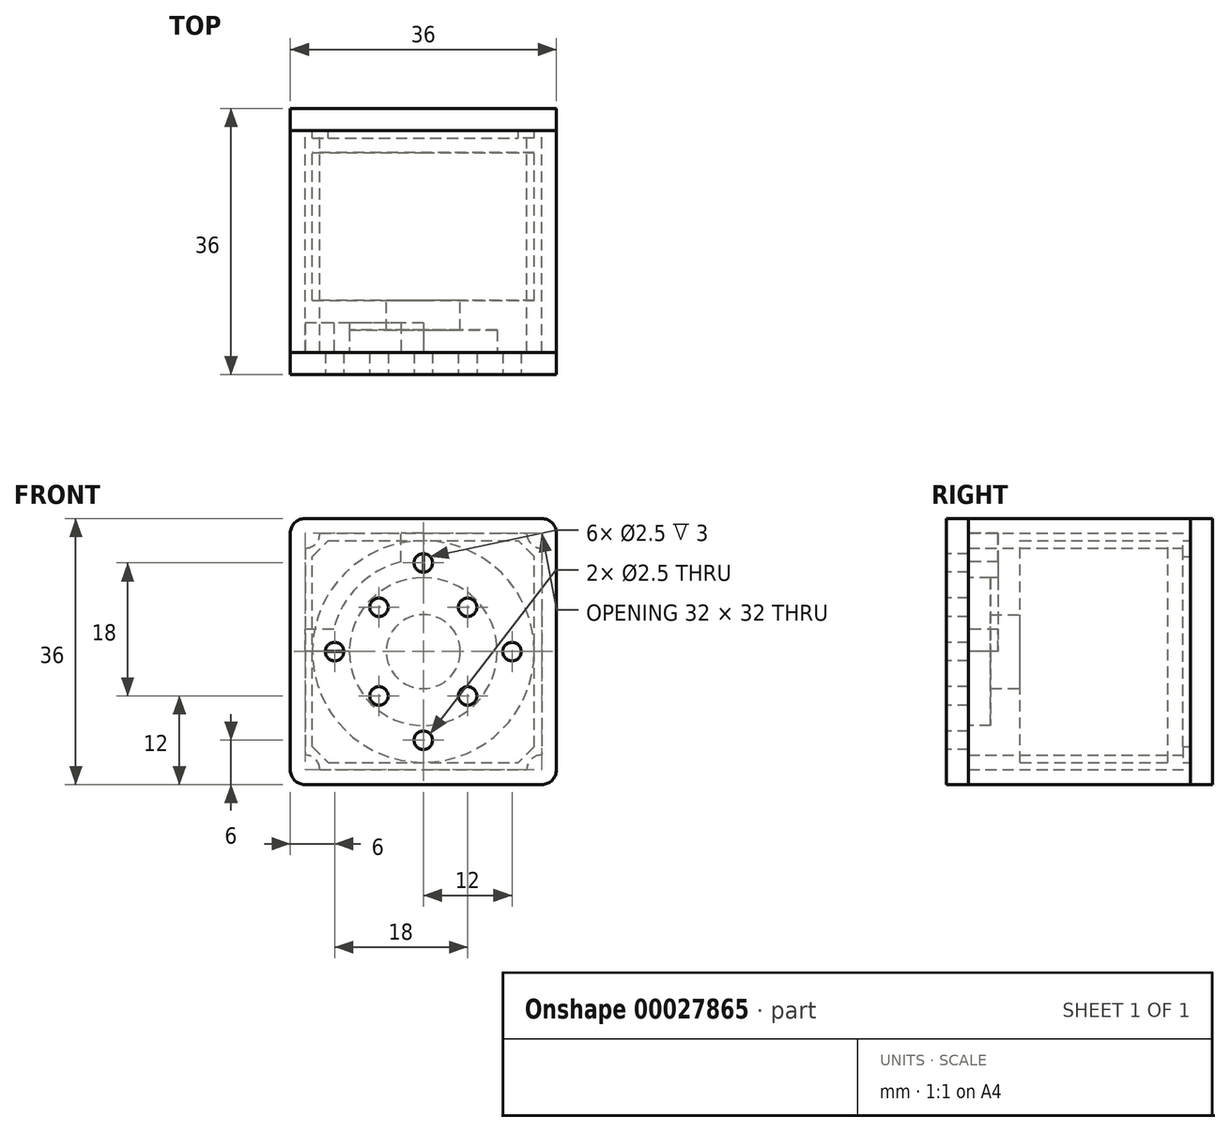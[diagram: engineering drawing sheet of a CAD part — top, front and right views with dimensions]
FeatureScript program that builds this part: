
annotation { "Feature Type Name" : "Feature", "Feature Type Description" : "" }
export const myFeature = defineFeature(function(context is Context, id is Id, definition is map)
    precondition{}
    {
        {
            var Q0;
            Q0=qCreatedBy(makeId("Front.planeOp"),FACE);
            var sketch = newSketch(context, id + "F0", { "sketchPlane" : qUnion([Q0])});
            skLineSegment(sketch, "E0.rect.bottom", {"start": v(18, -18) * mm, "end": v(-18, -18) * mm});
            skLineSegment(sketch, "E0.rect.top", {"start": v(18, 18) * mm, "end": v(-18, 18) * mm});
            skLineSegment(sketch, "E0.rect.left", {"start": v(18, -18) * mm, "end": v(18, 18) * mm});
            skLineSegment(sketch, "E0.rect.right", {"start": v(-18, -18) * mm, "end": v(-18, 18) * mm});
            skPoint(sketch, "E0.rect.middle", {"position": v(0, 0) * mm});
            skCircle(sketch, "E1", {"center": v(0, 0) * mm, "radius": 8.49 * mm, "construction": true});
            skLineSegment(sketch, "E2.rect.bottom", {"start": v(-6, 6) * mm, "end": v(6, 6) * mm, "construction": true});
            skLineSegment(sketch, "E2.rect.top", {"start": v(-6, -6) * mm, "end": v(6, -6) * mm, "construction": true});
            skLineSegment(sketch, "E2.rect.left", {"start": v(-6, 6) * mm, "end": v(-6, -6) * mm, "construction": true});
            skLineSegment(sketch, "E2.rect.right", {"start": v(6, 6) * mm, "end": v(6, -6) * mm, "construction": true});
            skCircle(sketch, "E3", {"center": v(-6, 6) * mm, "radius": 1.25 * mm});
            skCircle(sketch, "E4", {"center": v(6, 6) * mm, "radius": 1.25 * mm});
            skCircle(sketch, "E5", {"center": v(6, -6) * mm, "radius": 1.25 * mm});
            skCircle(sketch, "E6", {"center": v(-6, -6) * mm, "radius": 1.25 * mm});
            skCircle(sketch, "E7", {"center": v(0, 0) * mm, "radius": 12 * mm, "construction": true});
            skCircle(sketch, "E8", {"center": v(0, 12) * mm, "radius": 1.25 * mm});
            skCircle(sketch, "E9.1.0", {"center": v(-12, 0) * mm, "radius": 1.25 * mm});
            skCircle(sketch, "E9.2.0", {"center": v(0, -12) * mm, "radius": 1.25 * mm});
            skCircle(sketch, "E9.3.0", {"center": v(12, 0) * mm, "radius": 1.25 * mm});
            skCircle(sketch, "E10", {"center": v(0, 0) * mm, "radius": 15 * mm});
            skSolve(sketch);
        }
        {
            var Q0;
            Q0=qCreatedBy(makeId("Front.planeOp"),FACE);
            var sketch = newSketch(context, id + "F1", { "sketchPlane" : qUnion([Q0])});
            skLineSegment(sketch, "E11.rect.bottom", {"start": v(-16, 18) * mm, "end": v(0, 18) * mm});
            skLineSegment(sketch, "E11.rect.left", {"start": v(-18, 16) * mm, "end": v(-18, 0) * mm});
            skPoint(sketch, "E11.rect.middle", {"position": v(0, 0) * mm});
            skLineSegment(sketch, "E12.0", {"start": v(0, 16) * mm, "end": v(-14, 16) * mm});
            skLineSegment(sketch, "E12.3", {"start": v(-16, 0) * mm, "end": v(-16, 14) * mm});
            skArc(sketch, "E13", {"start": v(-16, 14) * mm, "mid": v(-14.59, 14.59) * mm, "end": v(-14, 16) * mm});
            skLineSegment(sketch, "E14", {"start": v(0, 18) * mm, "end": v(0, 0) * mm, "construction": true});
            skLineSegment(sketch, "E15", {"start": v(-18, 0) * mm, "end": v(0, 0) * mm, "construction": true});
            skPoint(sketch, "E16.visualSharp", {"position": v(-18, 18) * mm});
            skArc(sketch, "E16.filletArc", {"start": v(-16, 18) * mm, "mid": v(-17.41, 17.41) * mm, "end": v(-18, 16) * mm});
            skLineSegment(sketch, "E17", {"start": v(0, 18) * mm, "end": v(0, 16) * mm});
            skLineSegment(sketch, "E18", {"start": v(-18, 0) * mm, "end": v(-16, 0) * mm});
            skSolve(sketch);
        }
        {
            var Q0;
            Q0=qCreatedBy(makeId("Front.planeOp"),FACE);
            var sketch = newSketch(context, id + "F2", { "sketchPlane" : qUnion([Q0])});
            skArc(sketch, "E19", {"start": v(-7.07, 7.07) * mm, "mid": v(-9.24, 3.83) * mm, "end": v(-10, 0) * mm});
            skArc(sketch, "E20", {"start": v(-8.84, 8.84) * mm, "mid": v(-10.89, 6.14) * mm, "end": v(-12.13, 3) * mm});
            skLineSegment(sketch, "E21", {"start": v(-12.13, 3) * mm, "end": v(-16, 3) * mm});
            skLineSegment(sketch, "E22", {"start": v(-16, 0) * mm, "end": v(-16, 3) * mm});
            skLineSegment(sketch, "E23", {"start": v(-16, 16) * mm, "end": v(0, 0) * mm, "construction": true});
            skLineSegment(sketch, "E24", {"start": v(-16, 0) * mm, "end": v(0, 0) * mm, "construction": true});
            skArc(sketch, "E25.0.MirrorCS", {"start": v(-8.84, 8.84) * mm, "mid": v(-6.14, 10.89) * mm, "end": v(-3, 12.13) * mm});
            skLineSegment(sketch, "E26.0.MirrorCS", {"start": v(-3, 12.13) * mm, "end": v(-3, 16) * mm});
            skLineSegment(sketch, "E27.0.MirrorCS", {"start": v(0, 16) * mm, "end": v(-3, 16) * mm});
            skArc(sketch, "E28.0.MirrorCS", {"start": v(-7.07, 7.07) * mm, "mid": v(-3.83, 9.24) * mm, "end": v(0, 10) * mm});
            skLineSegment(sketch, "E29", {"start": v(0, 16) * mm, "end": v(0, 10) * mm});
            skLineSegment(sketch, "E30", {"start": v(-10, 0) * mm, "end": v(-16, 0) * mm});
            skSolve(sketch);
        }
        {
            var Q0;
            Q0=qSketchRegion(id+"F1",true);
            extrude(context, id + "F3", {"entities" : qUnion([Q0]), "endBound" : BoundingType.SYMMETRIC, "depth" : 30 * mm});
        }
        {
            var Q0;
            Q0=makeQuery(id+"F3.opExtrude","CAP_FACE",FACE,{"disambiguationData":[OSD([sQuery(id+"F1.wireOp",EDGE,"E11.rect.bottom"),sQuery(id+"F1.wireOp",EDGE,"E11.rect.left"),sQuery(id+"F1.wireOp",EDGE,"E12.0"),sQuery(id+"F1.wireOp",EDGE,"E12.3"),sQuery(id+"F1.wireOp",EDGE,"E13"),sQuery(id+"F1.wireOp",EDGE,"E16.filletArc"),sQuery(id+"F1.wireOp",EDGE,"E17"),sQuery(id+"F1.wireOp",EDGE,"E18")])],"isStart":false});
            var sketch = newSketch(context, id + "F4", { "sketchPlane" : qUnion([Q0])});
            skArc(sketch, "E31.0.0", {"start": v(-7.07, 7.07) * mm, "mid": v(-9.24, 3.83) * mm, "end": v(-10, 0) * mm});
            skArc(sketch, "E31.0.1", {"start": v(-7.07, 7.07) * mm, "mid": v(-3.83, 9.24) * mm, "end": v(0, 10) * mm});
            skLineSegment(sketch, "E31.0.2", {"start": v(0, 16) * mm, "end": v(0, 10) * mm});
            skLineSegment(sketch, "E31.0.3", {"start": v(0, 16) * mm, "end": v(-3, 16) * mm});
            skLineSegment(sketch, "E31.0.4", {"start": v(-3, 12.13) * mm, "end": v(-3, 16) * mm});
            skArc(sketch, "E31.0.5", {"start": v(-8.84, 8.84) * mm, "mid": v(-6.14, 10.89) * mm, "end": v(-3, 12.13) * mm});
            skArc(sketch, "E31.0.6", {"start": v(-8.84, 8.84) * mm, "mid": v(-10.89, 6.14) * mm, "end": v(-12.13, 3) * mm});
            skLineSegment(sketch, "E31.0.7", {"start": v(-12.13, 3) * mm, "end": v(-16, 3) * mm});
            skLineSegment(sketch, "E31.0.8", {"start": v(-16, 0) * mm, "end": v(-16, 3) * mm});
            skLineSegment(sketch, "E31.0.9", {"start": v(-10, 0) * mm, "end": v(-16, 0) * mm});
            skSolve(sketch);
        }
        {
            var Q0;
            Q0=qSketchRegion(id+"F4",true);
            extrude(context, id + "F5", {"entities" : qUnion([Q0]), "oppositeDirection" : true, "depth" : 4 * mm});
        }
        {
            var Q0;
            Q0=makeQuery(id+"F3.opExtrude","CAP_FACE",FACE,{"disambiguationData":[OSD([sQuery(id+"F1.wireOp",EDGE,"E11.rect.bottom"),sQuery(id+"F1.wireOp",EDGE,"E11.rect.left"),sQuery(id+"F1.wireOp",EDGE,"E12.0"),sQuery(id+"F1.wireOp",EDGE,"E12.3"),sQuery(id+"F1.wireOp",EDGE,"E13"),sQuery(id+"F1.wireOp",EDGE,"E16.filletArc"),sQuery(id+"F1.wireOp",EDGE,"E17"),sQuery(id+"F1.wireOp",EDGE,"E18")])],"isStart":true});
            var sketch = newSketch(context, id + "F6", { "sketchPlane" : qUnion([Q0])});
            skLineSegment(sketch, "E32", {"start": v(15, 0) * mm, "end": v(15, 12.88) * mm});
            skLineSegment(sketch, "E33", {"start": v(15, 12.88) * mm, "end": v(12.88, 15) * mm});
            skLineSegment(sketch, "E34", {"start": v(0, 15) * mm, "end": v(12.88, 15) * mm});
            skLineSegment(sketch, "E35", {"start": v(0, 15) * mm, "end": v(0, 0) * mm});
            skLineSegment(sketch, "E36", {"start": v(0, 0) * mm, "end": v(15, 0) * mm});
            skSolve(sketch);
        }
        {
            var Q0;
            Q0=qSketchRegion(id+"F6",true);
            extrude(context, id + "F7", {"entities" : qUnion([Q0]), "oppositeDirection" : true, "depth" : 1 * mm});
        }
        {
            var Q0;
            Q0=makeQuery(id+"F3.opExtrude","SWEPT_BODY",BODY,{"disambiguationData":[OSD([sQuery(id+"F1.wireOp",EDGE,"E11.rect.bottom"),sQuery(id+"F1.wireOp",EDGE,"E11.rect.left"),sQuery(id+"F1.wireOp",EDGE,"E12.0"),sQuery(id+"F1.wireOp",EDGE,"E12.3"),sQuery(id+"F1.wireOp",EDGE,"E13"),sQuery(id+"F1.wireOp",EDGE,"E16.filletArc"),sQuery(id+"F1.wireOp",EDGE,"E17"),sQuery(id+"F1.wireOp",EDGE,"E18")])]});
            var Q1;
            Q1=makeQuery(id+"F7.opExtrude","SWEPT_BODY",BODY,{"disambiguationData":[OSD([sQuery(id+"F6.wireOp",EDGE,"E32"),sQuery(id+"F6.wireOp",EDGE,"E33"),sQuery(id+"F6.wireOp",EDGE,"E34"),sQuery(id+"F6.wireOp",EDGE,"E35"),sQuery(id+"F6.wireOp",EDGE,"E36")])]});
            var Q2;
            Q2=qCreatedBy(makeId("Right.planeOp"),FACE);
            mirror(context, id + "F8", {"entities" : qUnion([Q0, Q1]), "mirrorPlane" : qUnion([Q2])});
        }
        {
            var Q0;
            Q0=makeQuery(id+"F8.opPattern","COPY",BODY,{"derivedFrom":makeQuery(id+"F3.opExtrude","SWEPT_BODY",BODY,{"disambiguationData":[OSD([sQuery(id+"F1.wireOp",EDGE,"E11.rect.bottom"),sQuery(id+"F1.wireOp",EDGE,"E11.rect.left"),sQuery(id+"F1.wireOp",EDGE,"E12.0"),sQuery(id+"F1.wireOp",EDGE,"E12.3"),sQuery(id+"F1.wireOp",EDGE,"E13"),sQuery(id+"F1.wireOp",EDGE,"E16.filletArc"),sQuery(id+"F1.wireOp",EDGE,"E17"),sQuery(id+"F1.wireOp",EDGE,"E18")])]}),"instanceName":"1"});
            var Q1;
            Q1=makeQuery(id+"F3.opExtrude","SWEPT_BODY",BODY,{"disambiguationData":[OSD([sQuery(id+"F1.wireOp",EDGE,"E11.rect.bottom"),sQuery(id+"F1.wireOp",EDGE,"E11.rect.left"),sQuery(id+"F1.wireOp",EDGE,"E12.0"),sQuery(id+"F1.wireOp",EDGE,"E12.3"),sQuery(id+"F1.wireOp",EDGE,"E13"),sQuery(id+"F1.wireOp",EDGE,"E16.filletArc"),sQuery(id+"F1.wireOp",EDGE,"E17"),sQuery(id+"F1.wireOp",EDGE,"E18")])]});
            var Q2;
            Q2=makeQuery(id+"F8.opPattern","COPY",BODY,{"derivedFrom":makeQuery(id+"F7.opExtrude","SWEPT_BODY",BODY,{"disambiguationData":[OSD([sQuery(id+"F6.wireOp",EDGE,"E32"),sQuery(id+"F6.wireOp",EDGE,"E33"),sQuery(id+"F6.wireOp",EDGE,"E34"),sQuery(id+"F6.wireOp",EDGE,"E35"),sQuery(id+"F6.wireOp",EDGE,"E36")])]}),"instanceName":"1"});
            var Q3;
            Q3=makeQuery(id+"F7.opExtrude","SWEPT_BODY",BODY,{"disambiguationData":[OSD([sQuery(id+"F6.wireOp",EDGE,"E32"),sQuery(id+"F6.wireOp",EDGE,"E33"),sQuery(id+"F6.wireOp",EDGE,"E34"),sQuery(id+"F6.wireOp",EDGE,"E35"),sQuery(id+"F6.wireOp",EDGE,"E36")])]});
            booleanBodies(context, id + "F9", {"operationType" : BooleanOperationType.UNION, "tools" : qUnion([Q0, Q1, Q2, Q3])});
        }
        {
            var Q0;
            Q0=makeQuery(id+"F8.opPattern","COPY",BODY,{"derivedFrom":makeQuery(id+"F3.opExtrude","SWEPT_BODY",BODY,{"disambiguationData":[OSD([sQuery(id+"F1.wireOp",EDGE,"E11.rect.bottom"),sQuery(id+"F1.wireOp",EDGE,"E11.rect.left"),sQuery(id+"F1.wireOp",EDGE,"E12.0"),sQuery(id+"F1.wireOp",EDGE,"E12.3"),sQuery(id+"F1.wireOp",EDGE,"E13"),sQuery(id+"F1.wireOp",EDGE,"E16.filletArc"),sQuery(id+"F1.wireOp",EDGE,"E17"),sQuery(id+"F1.wireOp",EDGE,"E18")])]}),"instanceName":"1"});
            var Q1;
            Q1=makeQuery(id+"F8.opPattern","COPY",BODY,{"derivedFrom":makeQuery(id+"F7.opExtrude","SWEPT_BODY",BODY,{"disambiguationData":[OSD([sQuery(id+"F6.wireOp",EDGE,"E32"),sQuery(id+"F6.wireOp",EDGE,"E33"),sQuery(id+"F6.wireOp",EDGE,"E34"),sQuery(id+"F6.wireOp",EDGE,"E35"),sQuery(id+"F6.wireOp",EDGE,"E36")])]}),"instanceName":"1"});
            var Q2;
            Q2=qCreatedBy(makeId("Top.planeOp"),FACE);
            mirror(context, id + "F10", {"entities" : qUnion([Q0, Q1]), "mirrorPlane" : qUnion([Q2])});
        }
        {
            var Q0;
            Q0=makeQuery(id+"F10.opPattern","COPY",BODY,{"derivedFrom":makeQuery(id+"F8.opPattern","COPY",BODY,{"derivedFrom":makeQuery(id+"F3.opExtrude","SWEPT_BODY",BODY,{"disambiguationData":[OSD([sQuery(id+"F1.wireOp",EDGE,"E11.rect.bottom"),sQuery(id+"F1.wireOp",EDGE,"E11.rect.left"),sQuery(id+"F1.wireOp",EDGE,"E12.0"),sQuery(id+"F1.wireOp",EDGE,"E12.3"),sQuery(id+"F1.wireOp",EDGE,"E13"),sQuery(id+"F1.wireOp",EDGE,"E16.filletArc"),sQuery(id+"F1.wireOp",EDGE,"E17"),sQuery(id+"F1.wireOp",EDGE,"E18")])]}),"instanceName":"1"}),"instanceName":"1"});
            var Q1;
            Q1=makeQuery(id+"F8.opPattern","COPY",BODY,{"derivedFrom":makeQuery(id+"F3.opExtrude","SWEPT_BODY",BODY,{"disambiguationData":[OSD([sQuery(id+"F1.wireOp",EDGE,"E11.rect.bottom"),sQuery(id+"F1.wireOp",EDGE,"E11.rect.left"),sQuery(id+"F1.wireOp",EDGE,"E12.0"),sQuery(id+"F1.wireOp",EDGE,"E12.3"),sQuery(id+"F1.wireOp",EDGE,"E13"),sQuery(id+"F1.wireOp",EDGE,"E16.filletArc"),sQuery(id+"F1.wireOp",EDGE,"E17"),sQuery(id+"F1.wireOp",EDGE,"E18")])]}),"instanceName":"1"});
            var Q2;
            Q2=makeQuery(id+"F8.opPattern","COPY",BODY,{"derivedFrom":makeQuery(id+"F7.opExtrude","SWEPT_BODY",BODY,{"disambiguationData":[OSD([sQuery(id+"F6.wireOp",EDGE,"E32"),sQuery(id+"F6.wireOp",EDGE,"E33"),sQuery(id+"F6.wireOp",EDGE,"E34"),sQuery(id+"F6.wireOp",EDGE,"E35"),sQuery(id+"F6.wireOp",EDGE,"E36")])]}),"instanceName":"1"});
            var Q3;
            Q3=makeQuery(id+"F10.opPattern","COPY",BODY,{"derivedFrom":makeQuery(id+"F8.opPattern","COPY",BODY,{"derivedFrom":makeQuery(id+"F7.opExtrude","SWEPT_BODY",BODY,{"disambiguationData":[OSD([sQuery(id+"F6.wireOp",EDGE,"E32"),sQuery(id+"F6.wireOp",EDGE,"E33"),sQuery(id+"F6.wireOp",EDGE,"E34"),sQuery(id+"F6.wireOp",EDGE,"E35"),sQuery(id+"F6.wireOp",EDGE,"E36")])]}),"instanceName":"1"}),"instanceName":"1"});
            booleanBodies(context, id + "F11", {"operationType" : BooleanOperationType.UNION, "tools" : qUnion([Q0, Q1, Q2, Q3])});
        }
        {
            var Q0;
            {var subQ0=makeQuery(id+"F3.opExtrude","CAP_FACE",FACE,{"disambiguationData":[OSD([sQuery(id+"F1.wireOp",EDGE,"E11.rect.bottom"),sQuery(id+"F1.wireOp",EDGE,"E11.rect.left"),sQuery(id+"F1.wireOp",EDGE,"E12.0"),sQuery(id+"F1.wireOp",EDGE,"E12.3"),sQuery(id+"F1.wireOp",EDGE,"E13"),sQuery(id+"F1.wireOp",EDGE,"E16.filletArc"),sQuery(id+"F1.wireOp",EDGE,"E17"),sQuery(id+"F1.wireOp",EDGE,"E18")])],"isStart":true});var subQ1=makeQuery(id+"F9.opBoolean","MERGE",FACE,{"derivedFrom":[subQ0,makeQuery(id+"F8.opPattern","COPY",FACE,{"derivedFrom":subQ0,"instanceName":"1"})]});Q0=makeQuery(id+"F11.opBoolean","MERGE",FACE,{"derivedFrom":[subQ1,makeQuery(id+"F10.opPattern","COPY",FACE,{"derivedFrom":subQ1,"instanceName":"1"})]});}
            var sketch = newSketch(context, id + "F12", { "sketchPlane" : qUnion([Q0])});
            skLineSegment(sketch, "E37.0.0", {"start": v(-16, -18) * mm, "end": v(16, -18) * mm});
            skArc(sketch, "E37.0.1", {"start": v(16, -18) * mm, "mid": v(17.41, -17.41) * mm, "end": v(18, -16) * mm});
            skLineSegment(sketch, "E37.0.2", {"start": v(18, -16) * mm, "end": v(18, 16) * mm});
            skArc(sketch, "E37.0.3", {"start": v(16, 18) * mm, "mid": v(17.41, 17.41) * mm, "end": v(18, 16) * mm});
            skLineSegment(sketch, "E37.0.4", {"start": v(-16, 18) * mm, "end": v(16, 18) * mm});
            skArc(sketch, "E37.0.5", {"start": v(-16, 18) * mm, "mid": v(-17.41, 17.41) * mm, "end": v(-18, 16) * mm});
            skLineSegment(sketch, "E37.0.6", {"start": v(-18, -16) * mm, "end": v(-18, 16) * mm});
            skArc(sketch, "E37.0.7", {"start": v(-16, -18) * mm, "mid": v(-17.41, -17.41) * mm, "end": v(-18, -16) * mm});
            skSolve(sketch);
        }
        {
            var Q0;
            Q0=qSketchRegion(id+"F12",true);
            extrude(context, id + "F13", {"entities" : qUnion([Q0]), "depth" : 3 * mm});
        }
        {
            var Q0;
            Q0=qCreatedBy(makeId("Front.planeOp"),FACE);
            cPlane(context, id + "F14", {"entities" : qUnion([Q0]), "cplaneType" : CPlaneType.OFFSET, "offset" : 12 * mm, "oppositeDirection" : true, "width" : 150 * mm, "height" : 150 * mm});
        }
        {
            var Q0;
            Q0=qCreatedBy(id+"F14.planeOp",FACE);
            var sketch = newSketch(context, id + "F15", { "sketchPlane" : qUnion([Q0])});
            skCircle(sketch, "E38", {"center": v(0, 0) * mm, "radius": 15 * mm});
            skSolve(sketch);
        }
        {
            var Q0;
            Q0=qSketchRegion(id+"F15",true);
            extrude(context, id + "F16", {"entities" : qUnion([Q0]), "depth" : 20 * mm});
        }
        {
            var Q0;
            {var subQ0=makeQuery(id+"F5.boolean.opBoolean","MERGE",FACE,{"derivedFrom":[makeQuery(id+"F3.opExtrude","CAP_FACE",FACE,{"disambiguationData":[OSD([sQuery(id+"F1.wireOp",EDGE,"E11.rect.bottom"),sQuery(id+"F1.wireOp",EDGE,"E11.rect.left"),sQuery(id+"F1.wireOp",EDGE,"E12.0"),sQuery(id+"F1.wireOp",EDGE,"E12.3"),sQuery(id+"F1.wireOp",EDGE,"E13"),sQuery(id+"F1.wireOp",EDGE,"E16.filletArc"),sQuery(id+"F1.wireOp",EDGE,"E17"),sQuery(id+"F1.wireOp",EDGE,"E18")])],"isStart":false}),makeQuery(id+"F5.opExtrude","CAP_FACE",FACE,{"disambiguationData":[OSD([sQuery(id+"F4.wireOp",EDGE,"E31.0.0"),sQuery(id+"F4.wireOp",EDGE,"E31.0.1"),sQuery(id+"F4.wireOp",EDGE,"E31.0.2"),sQuery(id+"F4.wireOp",EDGE,"E31.0.3"),sQuery(id+"F4.wireOp",EDGE,"E31.0.4"),sQuery(id+"F4.wireOp",EDGE,"E31.0.5"),sQuery(id+"F4.wireOp",EDGE,"E31.0.6"),sQuery(id+"F4.wireOp",EDGE,"E31.0.7"),sQuery(id+"F4.wireOp",EDGE,"E31.0.8"),sQuery(id+"F4.wireOp",EDGE,"E31.0.9")])],"isStart":true})]});var subQ1=makeQuery(id+"F9.opBoolean","MERGE",FACE,{"derivedFrom":[subQ0,makeQuery(id+"F8.opPattern","COPY",FACE,{"derivedFrom":subQ0,"instanceName":"1"})]});Q0=makeQuery(id+"F11.opBoolean","MERGE",FACE,{"derivedFrom":[subQ1,makeQuery(id+"F10.opPattern","COPY",FACE,{"derivedFrom":subQ1,"instanceName":"1"})]});}
            var sketch = newSketch(context, id + "F17", { "sketchPlane" : qUnion([Q0])});
            skCircle(sketch, "E39", {"center": v(0, 0) * mm, "radius": 10 * mm});
            skCircle(sketch, "E40", {"center": v(0, 0) * mm, "radius": 5 * mm});
            skSolve(sketch);
        }
        {
            var Q0;
            Q0=qSketchRegion(id+"F17",true);
            extrude(context, id + "F18", {"entities" : qUnion([Q0]), "oppositeDirection" : true, "depth" : 3 * mm});
        }
        {
            var Q0;
            Q0=qCreatedBy(makeId("Front.planeOp"),FACE);
            cPlane(context, id + "F19", {"entities" : qUnion([Q0]), "cplaneType" : CPlaneType.OFFSET, "offset" : 18 * mm, "width" : 150 * mm, "height" : 150 * mm});
        }
        {
            var Q0;
            Q0=makeQuery(id+"F16.opExtrude","CAP_FACE",FACE,{"disambiguationData":[OSD([sQuery(id+"F15.wireOp",EDGE,"E38")])],"isStart":false});
            var sketch = newSketch(context, id + "F20", { "sketchPlane" : qUnion([Q0])});
            skCircle(sketch, "E41", {"center": v(0, 0) * mm, "radius": 5 * mm});
            skSolve(sketch);
        }
        {
            var Q0;
            Q0=makeQuery(id+"F20.imprint","IMPRINT",FACE,{"disambiguationData":[TD([[makeQuery(id+"F20.imprint","IMPRINT",EDGE,{"derivedFrom":sQuery(id+"F20.wireOp",EDGE,"E41")}),1.0]])]});
            var Q1;
            Q1=sQuery(id+"F20.wireOp",EDGE,"E41");
            var Q2;
            Q2=qCreatedBy(id+"F19.planeOp",FACE);
            extrude(context, id + "F21", {"entities" : qUnion([Q0]), "surfaceEntities" : qUnion([Q1]), "endBound" : BoundingType.UP_TO_SURFACE, "endBoundEntityFace" : qUnion([Q2]), "depth" : 25 * mm});
        }
        {
            var Q0;
            Q0=qCreatedBy(id+"F19.planeOp",FACE);
            var sketch = newSketch(context, id + "F22", { "sketchPlane" : qUnion([Q0])});
            skLineSegment(sketch, "E42.0", {"start": v(16, -18) * mm, "end": v(-16, -18) * mm});
            skArc(sketch, "E42.1", {"start": v(-16, -18) * mm, "mid": v(-17.41, -17.41) * mm, "end": v(-18, -16) * mm});
            skLineSegment(sketch, "E42.2", {"start": v(-18, -16) * mm, "end": v(-18, 16) * mm});
            skArc(sketch, "E42.3", {"start": v(-16, 18) * mm, "mid": v(-17.41, 17.41) * mm, "end": v(-18, 16) * mm});
            skLineSegment(sketch, "E42.4", {"start": v(16, 18) * mm, "end": v(-16, 18) * mm});
            skArc(sketch, "E42.5", {"start": v(16, 18) * mm, "mid": v(17.41, 17.41) * mm, "end": v(18, 16) * mm});
            skLineSegment(sketch, "E42.6", {"start": v(18, -16) * mm, "end": v(18, 16) * mm});
            skArc(sketch, "E42.7", {"start": v(16, -18) * mm, "mid": v(17.41, -17.41) * mm, "end": v(18, -16) * mm});
            skCircle(sketch, "E43.0", {"center": v(0, 0) * mm, "radius": 15 * mm});
            skSolve(sketch);
        }
        {
            var Q0;
            Q0=qSketchRegion(id+"F22",true);
            var Q1;
            {var subQ0=makeQuery(id+"F5.boolean.opBoolean","MERGE",FACE,{"derivedFrom":[makeQuery(id+"F3.opExtrude","CAP_FACE",FACE,{"disambiguationData":[OSD([sQuery(id+"F1.wireOp",EDGE,"E11.rect.bottom"),sQuery(id+"F1.wireOp",EDGE,"E11.rect.left"),sQuery(id+"F1.wireOp",EDGE,"E12.0"),sQuery(id+"F1.wireOp",EDGE,"E12.3"),sQuery(id+"F1.wireOp",EDGE,"E13"),sQuery(id+"F1.wireOp",EDGE,"E16.filletArc"),sQuery(id+"F1.wireOp",EDGE,"E17"),sQuery(id+"F1.wireOp",EDGE,"E18")])],"isStart":false}),makeQuery(id+"F5.opExtrude","CAP_FACE",FACE,{"disambiguationData":[OSD([sQuery(id+"F4.wireOp",EDGE,"E31.0.0"),sQuery(id+"F4.wireOp",EDGE,"E31.0.1"),sQuery(id+"F4.wireOp",EDGE,"E31.0.2"),sQuery(id+"F4.wireOp",EDGE,"E31.0.3"),sQuery(id+"F4.wireOp",EDGE,"E31.0.4"),sQuery(id+"F4.wireOp",EDGE,"E31.0.5"),sQuery(id+"F4.wireOp",EDGE,"E31.0.6"),sQuery(id+"F4.wireOp",EDGE,"E31.0.7"),sQuery(id+"F4.wireOp",EDGE,"E31.0.8"),sQuery(id+"F4.wireOp",EDGE,"E31.0.9")])],"isStart":true})]});var subQ1=makeQuery(id+"F9.opBoolean","MERGE",FACE,{"derivedFrom":[subQ0,makeQuery(id+"F8.opPattern","COPY",FACE,{"derivedFrom":subQ0,"instanceName":"1"})]});Q1=makeQuery(id+"F11.opBoolean","MERGE",FACE,{"derivedFrom":[subQ1,makeQuery(id+"F10.opPattern","COPY",FACE,{"derivedFrom":subQ1,"instanceName":"1"})]});}
            extrude(context, id + "F23", {"entities" : qUnion([Q0]), "endBound" : BoundingType.UP_TO_SURFACE, "oppositeDirection" : true, "endBoundEntityFace" : qUnion([Q1]), "depth" : 25 * mm});
        }
        {
            var Q0;
            Q0=qCreatedBy(id+"F19.planeOp",FACE);
            var sketch = newSketch(context, id + "F24", { "sketchPlane" : qUnion([Q0])});
            skPoint(sketch, "E44.4", {"position": v(0, 0) * mm});
            skPoint(sketch, "E44.10", {"position": v(0, 0) * mm});
            skCircle(sketch, "E44.11", {"center": v(-6, 6) * mm, "radius": 1.25 * mm});
            skCircle(sketch, "E44.12", {"center": v(6, 6) * mm, "radius": 1.25 * mm});
            skCircle(sketch, "E44.13", {"center": v(6, -6) * mm, "radius": 1.25 * mm});
            skCircle(sketch, "E44.14", {"center": v(-6, -6) * mm, "radius": 1.25 * mm});
            skCircle(sketch, "E44.16", {"center": v(0, 12) * mm, "radius": 1.25 * mm});
            skCircle(sketch, "E44.17", {"center": v(-12, 0) * mm, "radius": 1.25 * mm});
            skCircle(sketch, "E44.18", {"center": v(0, -12) * mm, "radius": 1.25 * mm});
            skCircle(sketch, "E44.19", {"center": v(12, 0) * mm, "radius": 1.25 * mm});
            skPoint(sketch, "E44.20", {"position": v(0, 0) * mm});
            skCircle(sketch, "E44.21", {"center": v(0, 0) * mm, "radius": 15 * mm});
            skSolve(sketch);
        }
        {
            var Q0;
            Q0=qSketchRegion(id+"F24",true);
            var Q1;
            {var subQ0=makeQuery(id+"F5.boolean.opBoolean","MERGE",FACE,{"derivedFrom":[makeQuery(id+"F3.opExtrude","CAP_FACE",FACE,{"disambiguationData":[OSD([sQuery(id+"F1.wireOp",EDGE,"E11.rect.bottom"),sQuery(id+"F1.wireOp",EDGE,"E11.rect.left"),sQuery(id+"F1.wireOp",EDGE,"E12.0"),sQuery(id+"F1.wireOp",EDGE,"E12.3"),sQuery(id+"F1.wireOp",EDGE,"E13"),sQuery(id+"F1.wireOp",EDGE,"E16.filletArc"),sQuery(id+"F1.wireOp",EDGE,"E17"),sQuery(id+"F1.wireOp",EDGE,"E18")])],"isStart":false}),makeQuery(id+"F5.opExtrude","CAP_FACE",FACE,{"disambiguationData":[OSD([sQuery(id+"F4.wireOp",EDGE,"E31.0.0"),sQuery(id+"F4.wireOp",EDGE,"E31.0.1"),sQuery(id+"F4.wireOp",EDGE,"E31.0.2"),sQuery(id+"F4.wireOp",EDGE,"E31.0.3"),sQuery(id+"F4.wireOp",EDGE,"E31.0.4"),sQuery(id+"F4.wireOp",EDGE,"E31.0.5"),sQuery(id+"F4.wireOp",EDGE,"E31.0.6"),sQuery(id+"F4.wireOp",EDGE,"E31.0.7"),sQuery(id+"F4.wireOp",EDGE,"E31.0.8"),sQuery(id+"F4.wireOp",EDGE,"E31.0.9")])],"isStart":true})]});var subQ1=makeQuery(id+"F9.opBoolean","MERGE",FACE,{"derivedFrom":[subQ0,makeQuery(id+"F8.opPattern","COPY",FACE,{"derivedFrom":subQ0,"instanceName":"1"})]});Q1=makeQuery(id+"F11.opBoolean","MERGE",FACE,{"derivedFrom":[subQ1,makeQuery(id+"F10.opPattern","COPY",FACE,{"derivedFrom":subQ1,"instanceName":"1"})]});}
            extrude(context, id + "F25", {"entities" : qUnion([Q0]), "operationType" : NewBodyOperationType.ADD, "endBound" : BoundingType.UP_TO_SURFACE, "oppositeDirection" : true, "endBoundEntityFace" : qUnion([Q1]), "depth" : 25 * mm});
        }
    });
